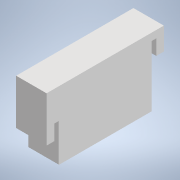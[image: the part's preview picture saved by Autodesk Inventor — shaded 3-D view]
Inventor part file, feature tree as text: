
AUTODESK INVENTOR PART (.ipt)
format: ipt  version: 2020 (Build 240168000, 168)  size: 112,640 bytes
history: native  units: in
note: dims shown in document units (in); Inventor stores cm internally (conversion verified against a paired STEP export)
features: reference x9, other x2, extrude x1, sketch x1
ambient origin geometry x8: Origin, YZ Plane, XZ Plane, XY Plane, X Axis, Y Axis, Z Axis, Center Point
bodies: Solid1 (feature_tree)
feature tree (13):
  extrude  "Extrusion1"  Depth=0.25in
  sketch  "Sketch1"  dims[d0=0.0118in d1=0.25in d2=0.0118in d3=0.0118in d4=0.0118in d5=0.0118in d6=0.25in d7=0.25in d8=0.5in d9=0.5in d10=1.0in d11=0.0in]
  reference  "Reference1"
  reference  "Reference2"
  reference  "Reference3"
  reference  "Reference4"
  reference  "Reference5"
  reference  "Reference6"
  reference  "Reference7"
  reference  "Reference8"
  reference  "Reference9"
  other  "Assembly1"
  other  "AM14U3 End Sheet Long:1"
